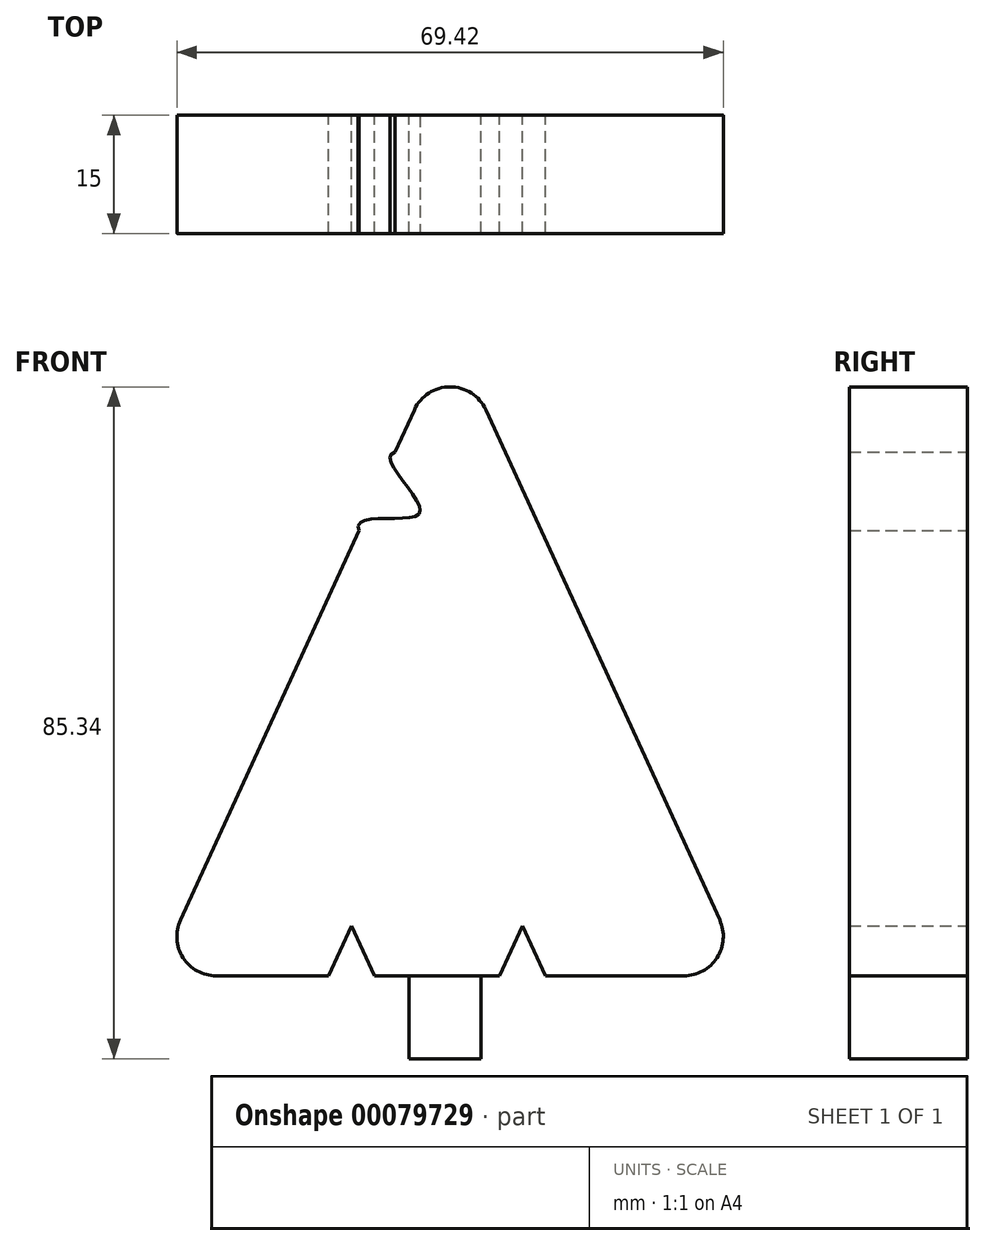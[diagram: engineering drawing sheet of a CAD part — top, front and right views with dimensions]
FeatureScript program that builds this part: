
annotation { "Feature Type Name" : "Feature", "Feature Type Description" : "" }
export const myFeature = defineFeature(function(context is Context, id is Id, definition is map)
    precondition{}
    {
        {
            var Q0;
            Q0=qCreatedBy(makeId("Front.planeOp"),FACE);
            var sketch = newSketch(context, id + "F0", { "sketchPlane" : qUnion([Q0])});
            skLineSegment(sketch, "E0.bottom", {"start": v(-14.4, -36.75) * mm, "end": v(-5.27, -36.75) * mm});
            skLineSegment(sketch, "E0.top", {"start": v(-14.4, -47.3) * mm, "end": v(-5.27, -47.3) * mm});
            skLineSegment(sketch, "E0.left", {"start": v(-14.4, -36.75) * mm, "end": v(-14.4, -47.3) * mm});
            skLineSegment(sketch, "E0.right", {"start": v(-5.27, -36.75) * mm, "end": v(-5.27, -47.3) * mm});
            skSolve(sketch);
        }
        {
            var Q0;
            Q0=qCreatedBy(makeId("Front.planeOp"),FACE);
            var sketch = newSketch(context, id + "F1", { "sketchPlane" : qUnion([Q0])});
            skLineSegment(sketch, "E1", {"start": v(-38.91, -36.77) * mm, "end": v(-24.62, -36.77) * mm});
            skLineSegment(sketch, "E2", {"start": v(-43.46, -29.69) * mm, "end": v(-20.78, 19.8) * mm});
            skLineSegment(sketch, "E3", {"start": v(-4.66, 35.13) * mm, "end": v(25.05, -29.69) * mm});
            skLineSegment(sketch, "E4", {"start": v(-18.79, -36.77) * mm, "end": v(-2.92, -36.77) * mm});
            skLineSegment(sketch, "E5", {"start": v(2.92, -36.77) * mm, "end": v(20.5, -36.77) * mm});
            skLineSegment(sketch, "E6", {"start": v(-24.62, -36.77) * mm, "end": v(-21.7, -30.4) * mm});
            skLineSegment(sketch, "E7", {"start": v(-21.7, -30.4) * mm, "end": v(-18.79, -36.77) * mm});
            skLineSegment(sketch, "E8.trimOffspring", {"start": v(-18.79, -36.77) * mm, "end": v(-9.2, -36.77) * mm});
            skPoint(sketch, "E9.orphan", {"position": v(-21.7, -36.77) * mm});
            skLineSegment(sketch, "E10", {"start": v(-2.92, -36.77) * mm, "end": v(0, -30.4) * mm});
            skLineSegment(sketch, "E11", {"start": v(0, -30.4) * mm, "end": v(2.92, -36.77) * mm});
            skPoint(sketch, "E12.trimOffspring.start.orphan", {"position": v(0, -36.77) * mm});
            skPoint(sketch, "E13.visualSharp", {"position": v(-9.2, 45.04) * mm});
            skArc(sketch, "E13.filletArc", {"start": v(-4.66, 35.13) * mm, "mid": v(-9.2, 38.04) * mm, "end": v(-13.75, 35.13) * mm});
            skPoint(sketch, "E14.visualSharp", {"position": v(28.3, -36.77) * mm});
            skArc(sketch, "E14.filletArc", {"start": v(20.5, -36.77) * mm, "mid": v(24.71, -34.47) * mm, "end": v(25.05, -29.69) * mm});
            skPoint(sketch, "E15.visualSharp", {"position": v(-46.7, -36.77) * mm});
            skArc(sketch, "E15.filletArc", {"start": v(-43.46, -29.69) * mm, "mid": v(-43.12, -34.47) * mm, "end": v(-38.91, -36.77) * mm});
            skLineSegment(sketch, "E16.bottom", {"start": v(-14, -36.77) * mm, "end": v(-6.21, -36.77) * mm});
            skPoint(sketch, "E17.end.orphan", {"position": v(-21.7, -39.61) * mm});
            skPoint(sketch, "E17.start.orphan", {"position": v(-46.7, -39.61) * mm});
            skFitSpline(sketch, "E18", {"points": [v(-20.78, 19.8) * mm, v(-13.06, 22.05) * mm, v(-16.22, 29.74) * mm], "startDerivative": vector(-6.64, 16.2) * mm, "endDerivative": vector(15.96, 3.56) * mm});
            skLineSegment(sketch, "E19.trimOffspring", {"start": v(-16.22, 29.74) * mm, "end": v(-13.75, 35.13) * mm});
            skSolve(sketch);
        }
        {
            var Q0;
            Q0 = qSketchRegion(id + "F1", true);
            extrude(context, id + "F2", {"entities" : qUnion([Q0]), "depth" : 15 * mm});
        }
        {
            var Q0;
            Q0=makeQuery(id+"F0.imprint","IMPRINT",FACE,{"disambiguationData":[TD([[makeQuery(id+"F0.imprint","IMPRINT",EDGE,{"derivedFrom":sQuery(id+"F0.wireOp",EDGE,"E0.bottom")}),-1.0]])]});
            extrude(context, id + "F3", {"entities" : qUnion([Q0]), "depth" : 15 * mm});
        }
    });
